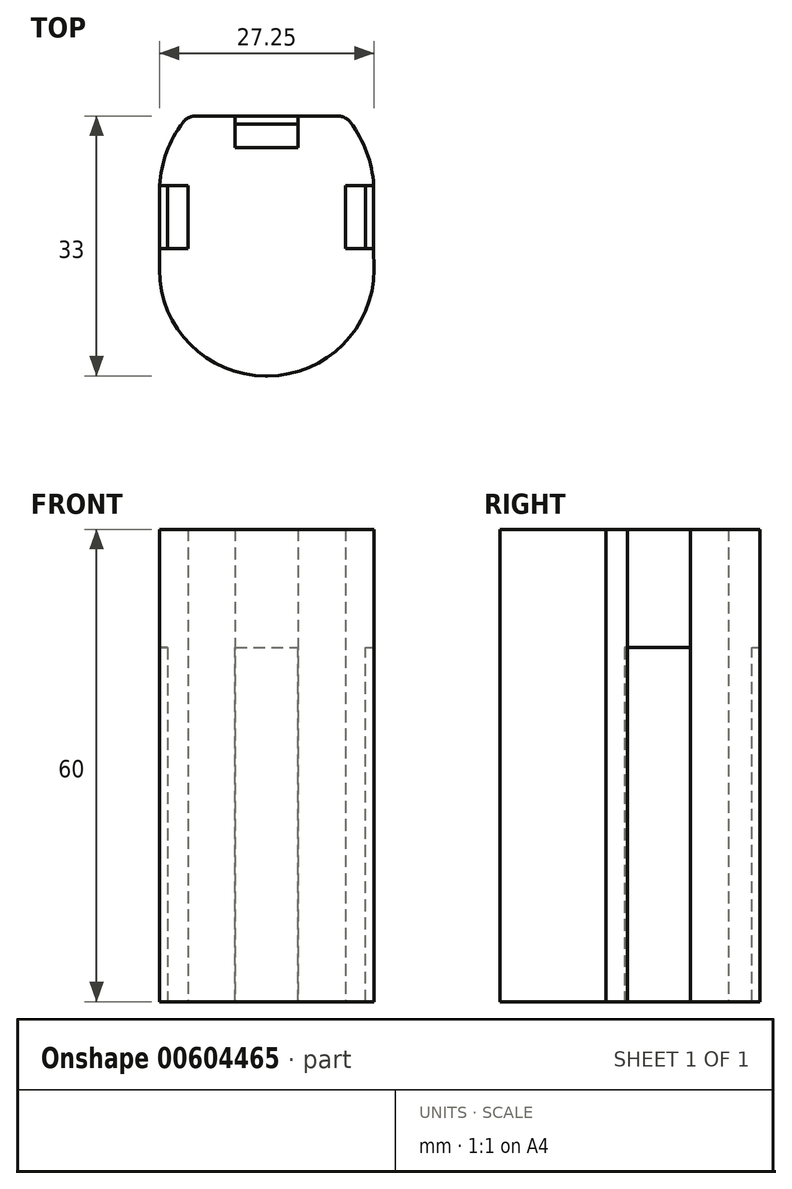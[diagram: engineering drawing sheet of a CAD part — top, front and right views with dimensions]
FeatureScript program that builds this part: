
annotation { "Feature Type Name" : "Feature", "Feature Type Description" : "" }
export const myFeature = defineFeature(function(context is Context, id is Id, definition is map)
    precondition{}
    {
        {
            var Q0;
            Q0=qCreatedBy(makeId("Top.planeOp"),FACE);
            var sketch = newSketch(context, id + "F0", { "sketchPlane" : qUnion([Q0])});
            skLineSegment(sketch, "E0", {"start": v(13.5, 0) * mm, "end": v(13.75, 0) * mm});
            skLineSegment(sketch, "E1", {"start": v(22.67, 33) * mm, "end": v(17.62, 33) * mm});
            skPoint(sketch, "E2.visualSharp", {"position": v(0, 0) * mm});
            skArc(sketch, "E2.filletArc", {"start": v(0, 13.5) * mm, "mid": v(3.95, 3.95) * mm, "end": v(13.5, 0) * mm});
            skPoint(sketch, "E3.visualSharp", {"position": v(27.25, 0) * mm});
            skArc(sketch, "E3.filletArc", {"start": v(13.75, 0) * mm, "mid": v(23.3, 3.95) * mm, "end": v(27.25, 13.5) * mm});
            skPoint(sketch, "E4.orphan", {"position": v(27.25, 33) * mm});
            skPoint(sketch, "E5.orphan", {"position": v(0, 33) * mm});
            skArc(sketch, "E6", {"start": v(0.03, 24.2) * mm, "mid": v(0.92, 28.41) * mm, "end": v(2.98, 32.2) * mm});
            skArc(sketch, "E7", {"start": v(27.22, 24.2) * mm, "mid": v(26.33, 28.41) * mm, "end": v(24.27, 32.2) * mm});
            skPoint(sketch, "E8.visualSharp", {"position": v(3.62, 33) * mm});
            skArc(sketch, "E8.filletArc", {"start": v(4.58, 33) * mm, "mid": v(3.69, 32.79) * mm, "end": v(2.98, 32.2) * mm});
            skPoint(sketch, "E9.visualSharp", {"position": v(23.62, 33) * mm});
            skArc(sketch, "E9.filletArc", {"start": v(24.27, 32.2) * mm, "mid": v(23.56, 32.79) * mm, "end": v(22.67, 33) * mm});
            skLineSegment(sketch, "E10.0", {"start": v(27.22, 24.2) * mm, "end": v(23.62, 24.2) * mm});
            skLineSegment(sketch, "E11.0", {"start": v(27.22, 16.2) * mm, "end": v(23.62, 16.2) * mm});
            skLineSegment(sketch, "E12.0", {"start": v(3.63, 24.2) * mm, "end": v(3.63, 16.2) * mm});
            skLineSegment(sketch, "E13.0", {"start": v(23.62, 16.2) * mm, "end": v(23.62, 24.2) * mm});
            skLineSegment(sketch, "E14.trimOffspring", {"start": v(3.62, 16.2) * mm, "end": v(0.03, 16.2) * mm});
            skLineSegment(sketch, "E15.trimOffspring", {"start": v(3.62, 24.2) * mm, "end": v(0.03, 24.2) * mm});
            skPoint(sketch, "E16.orphan", {"position": v(27.25, 23.25) * mm});
            skPoint(sketch, "E17.start.orphan", {"position": v(0, 23.25) * mm});
            skLineSegment(sketch, "E18", {"start": v(0, 13.5) * mm, "end": v(0.03, 16.2) * mm});
            skLineSegment(sketch, "E19", {"start": v(27.25, 13.5) * mm, "end": v(27.22, 16.2) * mm});
            skLineSegment(sketch, "E20.0", {"start": v(17.62, 29) * mm, "end": v(9.62, 29) * mm});
            skLineSegment(sketch, "E21.0", {"start": v(9.62, 33) * mm, "end": v(9.62, 29) * mm});
            skLineSegment(sketch, "E22.0", {"start": v(17.62, 33) * mm, "end": v(17.62, 29) * mm});
            skPoint(sketch, "E23.orphan", {"position": v(22.67, 29) * mm});
            skPoint(sketch, "E24.orphan", {"position": v(4.58, 29) * mm});
            skPoint(sketch, "E25.end.orphan", {"position": v(13.62, 29) * mm});
            skPoint(sketch, "E25.start.orphan", {"position": v(13.62, 33) * mm});
            skLineSegment(sketch, "E26.trimOffspring", {"start": v(9.62, 33) * mm, "end": v(4.58, 33) * mm});
            skSolve(sketch);
        }
        {
            var Q0;
            Q0=makeQuery(id+"F0.imprint","IMPRINT",FACE,{"disambiguationData":[TD([[makeQuery(id+"F0.imprint","IMPRINT",EDGE,{"derivedFrom":sQuery(id+"F0.wireOp",EDGE,"E0")}),1.0]])]});
            extrude(context, id + "F1", {"entities" : qUnion([Q0]), "depth" : 60 * mm, "offsetDistance" : 25 * mm});
        }
        {
            var Q0;
            Q0=makeQuery(id+"F1.opExtrude","CAP_FACE",FACE,{"disambiguationData":[OSD([sQuery(id+"F0.wireOp",EDGE,"E0"),sQuery(id+"F0.wireOp",EDGE,"E1"),sQuery(id+"F0.wireOp",EDGE,"E2.filletArc"),sQuery(id+"F0.wireOp",EDGE,"E3.filletArc"),sQuery(id+"F0.wireOp",EDGE,"E6"),sQuery(id+"F0.wireOp",EDGE,"E7"),sQuery(id+"F0.wireOp",EDGE,"E8.filletArc"),sQuery(id+"F0.wireOp",EDGE,"E9.filletArc"),sQuery(id+"F0.wireOp",EDGE,"E10.0"),sQuery(id+"F0.wireOp",EDGE,"E11.0"),sQuery(id+"F0.wireOp",EDGE,"E12.0"),sQuery(id+"F0.wireOp",EDGE,"E13.0"),sQuery(id+"F0.wireOp",EDGE,"E14.trimOffspring"),sQuery(id+"F0.wireOp",EDGE,"E15.trimOffspring"),sQuery(id+"F0.wireOp",EDGE,"E18"),sQuery(id+"F0.wireOp",EDGE,"E19"),sQuery(id+"F0.wireOp",EDGE,"E20.0"),sQuery(id+"F0.wireOp",EDGE,"E21.0"),sQuery(id+"F0.wireOp",EDGE,"E22.0"),sQuery(id+"F0.wireOp",EDGE,"E26.trimOffspring")])],"isStart":true});
            cPlane(context, id + "F2", {"entities" : qUnion([Q0]), "cplaneType" : CPlaneType.OFFSET, "offset" : 0 * mm, "width" : 150 * mm, "height" : 150 * mm});
        }
        {
            var Q0;
            Q0=qCreatedBy(id+"F2.planeOp",FACE);
            var sketch = newSketch(context, id + "F3", { "sketchPlane" : qUnion([Q0])});
            skLineSegment(sketch, "E27", {"start": v(27.2, -15.59) * mm, "end": v(27.2, -24.29) * mm});
            skLineSegment(sketch, "E28", {"start": v(27.2, -24.29) * mm, "end": v(26.2, -24.29) * mm});
            skLineSegment(sketch, "E29", {"start": v(26.2, -24.29) * mm, "end": v(26.2, -15.59) * mm});
            skLineSegment(sketch, "E30", {"start": v(26.2, -15.59) * mm, "end": v(27.2, -15.59) * mm});
            skLineSegment(sketch, "E31", {"start": v(0, -24.18) * mm, "end": v(0, -15.8) * mm});
            skLineSegment(sketch, "E32", {"start": v(0, -15.8) * mm, "end": v(1, -15.8) * mm});
            skLineSegment(sketch, "E33", {"start": v(1, -15.8) * mm, "end": v(1, -24.18) * mm});
            skLineSegment(sketch, "E34", {"start": v(1, -24.18) * mm, "end": v(0, -24.18) * mm});
            skLineSegment(sketch, "E35", {"start": v(9.41, -31.99) * mm, "end": v(17.97, -31.99) * mm});
            skLineSegment(sketch, "E36", {"start": v(17.97, -31.99) * mm, "end": v(17.97, -32.99) * mm});
            skLineSegment(sketch, "E37", {"start": v(17.97, -32.99) * mm, "end": v(9.27, -32.99) * mm});
            skLineSegment(sketch, "E38", {"start": v(9.27, -32.99) * mm, "end": v(9.41, -31.99) * mm});
            skSolve(sketch);
        }
        {
            var Q0;
            Q0=makeQuery(id+"F3.imprint","IMPRINT",FACE,{"disambiguationData":[TD([[makeQuery(id+"F3.imprint","IMPRINT",EDGE,{"derivedFrom":sQuery(id+"F3.wireOp",EDGE,"E31")}),-1.0]])]});
            var Q1;
            Q1=makeQuery(id+"F3.imprint","IMPRINT",FACE,{"disambiguationData":[TD([[makeQuery(id+"F3.imprint","IMPRINT",EDGE,{"derivedFrom":sQuery(id+"F3.wireOp",EDGE,"E27")}),-1.0]])]});
            var Q2;
            Q2=makeQuery(id+"F3.imprint","IMPRINT",FACE,{"disambiguationData":[TD([[makeQuery(id+"F3.imprint","IMPRINT",EDGE,{"derivedFrom":sQuery(id+"F3.wireOp",EDGE,"E35")}),-1.0]])]});
            extrude(context, id + "F4", {"entities" : qUnion([Q0, Q1, Q2]), "operationType" : NewBodyOperationType.ADD, "oppositeDirection" : true, "depth" : 45 * mm, "offsetDistance" : 25 * mm});
        }
    });
